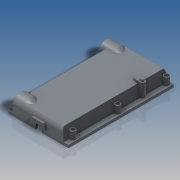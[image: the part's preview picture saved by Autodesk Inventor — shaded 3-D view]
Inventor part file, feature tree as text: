
AUTODESK INVENTOR PART (.ipt)
format: ipt  version: 2016 SP2 (Build 200236200, 236)  size: 784,896 bytes
history: native  units: in
note: dims shown in document units (in); Inventor stores cm internally (conversion verified against a paired STEP export)
features: extrude x22, sketch x15, plane x7, revolve x5, projected_geometry x3, fillet x2
ambient origin geometry x8: Origin, YZ Plane, XZ Plane, XY Plane, X Axis, Y Axis, Z Axis, Center Point
bodies: Solid1 (feature_tree)
feature tree (54):
  extrude  "Extrusion1"  Depth=0.0945in
  extrude  "Extrusion2"  Depth=0.1575in
  sketch  "Sketch4"  dims[d4=0.2362in d6=1.4803in]
  extrude  "Extrusion3"  Depth=1.4803in
  extrude  "Extrusion4"  Depth=0.5827in
  extrude  "Extrusion5"  Depth=0.4094in
  extrude  "Extrusion7"  Depth=0.4409in
  extrude  "Extrusion6"  Depth=0.378in
  extrude  "Extrusion8"  Depth=0.1575in TaperAngle=0.0deg
  sketch  "Sketch7"  dims[d10=0.0787in d11=0.4094in]
  plane  "Work Plane1"
  plane  "Work Plane2"
  extrude  "Extrusion11"  Depth=0.1102in TaperAngle=0.0deg
  extrude  "Extrusion14"  Depth=0.252in
  sketch  "Sketch9"  dims[d15=0.252in d16=0.378in]
  extrude  "Extrusion12"  Depth=0.189in
  extrude  "Extrusion13"  Depth=0.252in
  plane  "Work Plane3"
  sketch  "Sketch10"  dims[d17=0.2677in d18=0.1575in d19=0.0in]
  revolve  "Revolution1"  [1 undecoded]
  revolve  "Revolution2"  [1 undecoded]
  revolve  "Revolution3"  [1 undecoded]
  extrude  "Extrusion15"  Depth=0.0039in
  plane  "Work Plane4"
  sketch  "Sketch13"  dims[d28=0.2835in d29=0.189in]
  revolve  "Revolution4"  [1 undecoded]
  revolve  "Revolution5"  [1 undecoded]
  plane  "Work Plane5"
  sketch  "Sketch14"  dims[d30=0.2205in d31=0.0in d32=0.0in d33=0.252in]
  extrude  "Extrusion16"  Depth=0.0039in
  extrude  "Extrusion17"  Depth=0.0039in
  extrude  "Extrusion18"  TaperAngle=0.0deg  [1 undecoded]
  plane  "Work Plane6"
  sketch  "Sketch15"  dims[d34=0.0in d35=0.063in]
  extrude  "Extrusion19"  Depth=0.0039in
  extrude  "Extrusion20"  Depth=0.0039in
  extrude  "Extrusion21"  Depth=0.0039in
  extrude  "Extrusion22"  Depth=0.3937in
  plane  "Work Plane7"
  sketch  "Sketch17"  dims[d38=1.4488in d39=0.2047in d40=0.0315in d41=0.1102in d42=0.3937in d43=0.4252in d44=0.063in d45=0.0in d51=0.6558in d52=0.6372in d53=0.0472in d54=0.3937in d55=0.3937in d56=0.0in d57=0.0315in d58=0.3937in d59=0.0in d60=0.3937in d61=0.0in d62=0.315in d63=0.252in d64=0.4749in d65=1.0727in d66=90.0deg d67=90.0deg d68=90.0deg d69=0.3937in d70=0.0in d71=0.4749in d72=0.3937in d73=0.0in d74=90.0deg d75=90.0deg d76=0.0472in d77=0.8661in d79=0.189in d80=0.0787in d81=0.5354in d82=0.189in d83=0.1417in d84=0.378in d85=0.2835in d86=0.315in d87=0.0in d88=0.315in d89=0.0in d90=0.0315in d91=0.0in d92=0.252in d93=0.168in d94=0.126in d95=0.0945in d96=0.5984in d97=2.189in d98=0.252in d99=0.1102in d100=1.4488in d101=0.126in d102=0.0315in d103=0.0in d104=0.0945in d105=0.063in d106=0.0in d107=0.063in d108=0.0in d109=0.1102in d110=0.0in d111=0.4409in d112=0.1575in d113=0.8504in d114=0.2992in d115=0.1575in d116=0.0945in d117=0.1102in d118=0.0in d119=0.063in d120=0.0in d123=0.0039in d124=0.0039in]
  extrude  "Extrusion23"  Depth=0.3937in TaperAngle=0.0deg
  extrude  "Extrusion24"  Depth=0.0039in
  fillet  "Fillet3"  Radius=0.3937in
  fillet  "Fillet4"  Radius=0.3937in
  sketch  "Sketch2"  dims[d0=1.9528in d1=0.0945in]
  sketch  "Sketch3"  dims[d2=0.3672in d3=0.1575in]
  sketch  "Sketch5"  dims[d7=3.4016in d8=0.0in d9=0.5827in]
  sketch  "Sketch8"  dims[d12=0.0in d13=0.0in d14=0.4409in]
  sketch  "Sketch11"  dims[d20=0.1102in d21=0.2205in d22=0.0in d23=0.0in d24=0.1102in d25=0.0in]
  projected_geometry  "Projected Loop1"
  sketch  "Sketch12"  dims[d26=0.189in d27=0.252in]
  projected_geometry  "Projected Loop2"
  projected_geometry  "Projected Loop3"
  sketch  "Sketch16"  dims[d36=0.0315in d37=0.0472in]
note: 6 required parameter values undecoded (feature->parameter linkage not recoverable at this tier; creation-order binding heuristic only, values carry confidence <= 0.55)